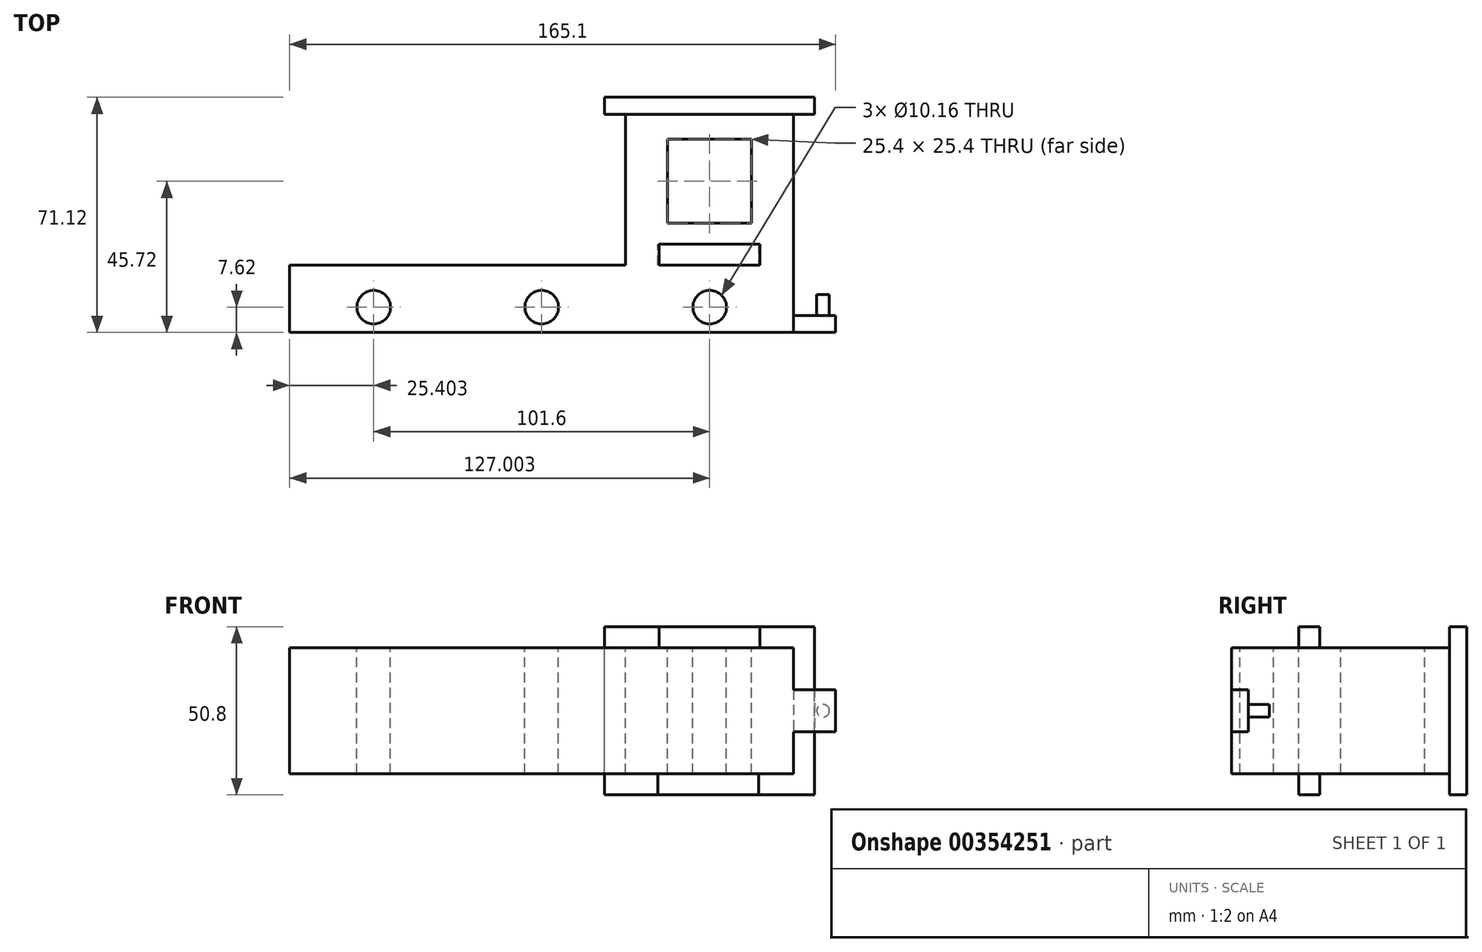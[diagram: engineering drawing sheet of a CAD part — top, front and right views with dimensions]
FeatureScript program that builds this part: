
annotation { "Feature Type Name" : "Feature", "Feature Type Description" : "" }
export const myFeature = defineFeature(function(context is Context, id is Id, definition is map)
    precondition{}
    {
        {
            var Q0;
            Q0=qCreatedBy(makeId("Front.planeOp"),FACE);
            var sketch = newSketch(context, id + "F0", { "sketchPlane" : qUnion([Q0])});
            skLineSegment(sketch, "E0.bottom", {"start": v(-68.46, 19.52) * mm, "end": v(83.94, 19.52) * mm});
            skLineSegment(sketch, "E0.top", {"start": v(-68.46, -18.58) * mm, "end": v(83.94, -18.58) * mm});
            skLineSegment(sketch, "E0.left", {"start": v(-68.46, 19.52) * mm, "end": v(-68.46, -18.58) * mm});
            skLineSegment(sketch, "E0.right", {"start": v(83.94, 19.52) * mm, "end": v(83.94, -18.58) * mm});
            skSolve(sketch);
        }
        {
            var Q0;
            Q0 = qSketchRegion(id + "F0", true);
            extrude(context, id + "F1", {"entities" : qUnion([Q0]), "depth" : 20.32 * mm});
        }
        {
            var Q0;
            Q0=makeQuery(id+"F1.opExtrude","CAP_FACE",FACE,{"disambiguationData":[OSD([sQuery(id+"F0.wireOp",EDGE,"E0.bottom"),sQuery(id+"F0.wireOp",EDGE,"E0.top"),sQuery(id+"F0.wireOp",EDGE,"E0.left"),sQuery(id+"F0.wireOp",EDGE,"E0.right")])],"isStart":true});
            var sketch = newSketch(context, id + "F2", { "sketchPlane" : qUnion([Q0])});
            skLineSegment(sketch, "E1", {"start": v(-33.14, -18.58) * mm, "end": v(-33.14, 19.52) * mm});
            skSolve(sketch);
        }
        {
            var Q0;
            {var subQ0=sQuery(id+"F2.wireOp",EDGE,"E1");Q0=makeQuery(id+"F2.imprint","IMPRINT",FACE,{"disambiguationData":[TD([[makeQuery(id+"F2.imprint","IMPRINT",EDGE,{"derivedFrom":subQ0}),1.0]])]});}
            extrude(context, id + "F3", {"entities" : qUnion([Q0]), "operationType" : NewBodyOperationType.ADD, "depth" : 50.8 * mm});
        }
        {
            var Q0;
            {var subQ0=sQuery(id+"F0.wireOp",EDGE,"E0.bottom");Q0=makeQuery(id+"F3.boolean.opBoolean","MERGE",FACE,{"derivedFrom":[makeQuery(id+"F1.opExtrude","SWEPT_FACE",FACE,{"disambiguationData":[OSD([subQ0])]}),makeQuery(id+"F3.opExtrude","SWEPT_FACE",FACE,{"disambiguationData":[OSD([subQ0])]})]});}
            var sketch = newSketch(context, id + "F4", { "sketchPlane" : qUnion([Q0])});
            skLineSegment(sketch, "E2.bottom", {"start": v(45.84, 38.1) * mm, "end": v(71.24, 38.1) * mm});
            skLineSegment(sketch, "E2.top", {"start": v(45.84, 12.7) * mm, "end": v(71.24, 12.7) * mm});
            skLineSegment(sketch, "E2.left", {"start": v(45.84, 38.1) * mm, "end": v(45.84, 12.7) * mm});
            skLineSegment(sketch, "E2.right", {"start": v(71.24, 38.1) * mm, "end": v(71.24, 12.7) * mm});
            skSolve(sketch);
        }
        {
            var Q0;
            Q0 = qSketchRegion(id + "F4", true);
            extrude(context, id + "F5", {"entities" : qUnion([Q0]), "operationType" : NewBodyOperationType.REMOVE, "endBound" : BoundingType.THROUGH_ALL, "oppositeDirection" : true, "depth" : 25.4 * mm});
        }
        {
            var Q0;
            {var subQ0=sQuery(id+"F0.wireOp",EDGE,"E0.bottom");Q0=makeQuery(id+"F3.boolean.opBoolean","MERGE",FACE,{"derivedFrom":[makeQuery(id+"F1.opExtrude","SWEPT_FACE",FACE,{"disambiguationData":[OSD([subQ0])]}),makeQuery(id+"F3.opExtrude","SWEPT_FACE",FACE,{"disambiguationData":[OSD([subQ0])]})]});}
            var sketch = newSketch(context, id + "F6", { "sketchPlane" : qUnion([Q0])});
            skLineSegment(sketch, "E3.top", {"start": v(43.3, 0) * mm, "end": v(73.78, 0) * mm});
            skLineSegment(sketch, "E4.MirrorCS", {"start": v(43.3, 6.35) * mm, "end": v(73.78, 6.35) * mm});
            skLineSegment(sketch, "E5.MirrorCS", {"start": v(43.3, 6.35) * mm, "end": v(43.3, 0) * mm});
            skLineSegment(sketch, "E6.MirrorCS", {"start": v(73.78, 6.35) * mm, "end": v(73.78, 0) * mm});
            skLineSegment(sketch, "E7", {"start": v(73.78, 0) * mm, "end": v(43.3, 0) * mm});
            skSolve(sketch);
        }
        {
            var Q0;
            Q0 = qSketchRegion(id + "F6", true);
            extrude(context, id + "F7", {"entities" : qUnion([Q0]), "operationType" : NewBodyOperationType.ADD, "depth" : 6.35 * mm});
        }
        {
            var Q0;
            {var subQ0=sQuery(id+"F0.wireOp",EDGE,"E0.top");Q0=makeQuery(id+"F3.boolean.opBoolean","MERGE",FACE,{"derivedFrom":[makeQuery(id+"F1.opExtrude","SWEPT_FACE",FACE,{"disambiguationData":[OSD([subQ0])]}),makeQuery(id+"F3.opExtrude","SWEPT_FACE",FACE,{"disambiguationData":[OSD([subQ0])]})]});}
            var sketch = newSketch(context, id + "F8", { "sketchPlane" : qUnion([Q0])});
            skLineSegment(sketch, "E8.MirrorCS", {"start": v(42.87, -6.35) * mm, "end": v(73.35, -6.35) * mm});
            skLineSegment(sketch, "E9.MirrorCS", {"start": v(42.87, 0) * mm, "end": v(42.87, -6.35) * mm});
            skLineSegment(sketch, "E10.MirrorCS", {"start": v(73.35, -6.35) * mm, "end": v(73.35, 0) * mm});
            skLineSegment(sketch, "E11", {"start": v(73.35, 0) * mm, "end": v(42.87, 0) * mm});
            skSolve(sketch);
        }
        {
            var Q0;
            Q0 = qSketchRegion(id + "F8", true);
            extrude(context, id + "F9", {"entities" : qUnion([Q0]), "operationType" : NewBodyOperationType.ADD, "depth" : 6.35 * mm});
        }
        {
            var Q0;
            {var subQ0=sQuery(id+"F0.wireOp",EDGE,"E0.right");Q0=makeQuery(id+"F3.boolean.opBoolean","MERGE",FACE,{"derivedFrom":[makeQuery(id+"F1.opExtrude","SWEPT_FACE",FACE,{"disambiguationData":[OSD([subQ0])]}),makeQuery(id+"F3.opExtrude","SWEPT_FACE",FACE,{"disambiguationData":[OSD([subQ0])]})]});}
            var sketch = newSketch(context, id + "F10", { "sketchPlane" : qUnion([Q0])});
            skLineSegment(sketch, "E12", {"start": v(45.65, -18.58) * mm, "end": v(45.65, 19.52) * mm});
            skSolve(sketch);
        }
        {
            var Q0;
            {var subQ0=sQuery(id+"F10.wireOp",EDGE,"E12");Q0=makeQuery(id+"F10.imprint","IMPRINT",FACE,{"disambiguationData":[TD([[makeQuery(id+"F10.imprint","IMPRINT",EDGE,{"derivedFrom":subQ0}),-1.0]])]});}
            extrude(context, id + "F11", {"entities" : qUnion([Q0]), "operationType" : NewBodyOperationType.ADD, "depth" : 6.35 * mm});
        }
        {
            var Q0;
            Q0=makeQuery(id+"F6.imprint","IMPRINT",FACE,{"disambiguationData":[TD([[makeQuery(id+"F6.imprint","IMPRINT",EDGE,{"derivedFrom":sQuery(id+"F6.wireOp",EDGE,"E4.MirrorCS")}),1.0]])]});
            var sketch = newSketch(context, id + "F12", { "sketchPlane" : qUnion([Q0])});
            skLineSegment(sketch, "E13", {"start": v(83.94, 45.65) * mm, "end": v(33.14, 45.65) * mm});
            skSolve(sketch);
        }
        {
            var Q0;
            {var subQ0=sQuery(id+"F12.wireOp",EDGE,"E13");Q0=makeQuery(id+"F12.imprint","IMPRINT",FACE,{"disambiguationData":[TD([[makeQuery(id+"F12.imprint","IMPRINT",EDGE,{"derivedFrom":subQ0}),-1.0]])]});}
            extrude(context, id + "F13", {"entities" : qUnion([Q0]), "operationType" : NewBodyOperationType.ADD, "depth" : 6.35 * mm});
        }
        {
            var Q0;
            Q0=makeQuery(id+"F13.opExtrude","SWEPT_FACE",FACE,{"disambiguationData":[OSD([sQuery(id+"F0.wireOp",EDGE,"E0.bottom"),sQuery(id+"F0.wireOp",EDGE,"E0.right")])]});
            extrude(context, id + "F14", {"entities" : qUnion([Q0]), "operationType" : NewBodyOperationType.ADD, "depth" : 6.35 * mm});
        }
        {
            var Q0;
            {var subQ0=sQuery(id+"F0.wireOp",EDGE,"E0.top");Q0=makeQuery(id+"F11.boolean.opBoolean","MERGE",FACE,{"derivedFrom":[makeQuery(id+"F3.boolean.opBoolean","MERGE",FACE,{"derivedFrom":[makeQuery(id+"F1.opExtrude","SWEPT_FACE",FACE,{"disambiguationData":[OSD([subQ0])]}),makeQuery(id+"F3.opExtrude","SWEPT_FACE",FACE,{"disambiguationData":[OSD([subQ0])]})]}),makeQuery(id+"F11.opExtrude","SWEPT_FACE",FACE,{"disambiguationData":[OSD([subQ0,sQuery(id+"F0.wireOp",EDGE,"E0.right")])]})]});}
            var sketch = newSketch(context, id + "F15", { "sketchPlane" : qUnion([Q0])});
            skLineSegment(sketch, "E14", {"start": v(83.94, -45.65) * mm, "end": v(33.14, -45.65) * mm});
            skSolve(sketch);
        }
        {
            var Q0;
            {var subQ3=sQuery(id+"F15.wireOp",EDGE,"E14");Q0=makeQuery(id+"F15.imprint","IMPRINT",FACE,{"disambiguationData":[TD([[makeQuery(id+"F15.imprint","IMPRINT",EDGE,{"derivedFrom":subQ3}),1.0]])]});}
            extrude(context, id + "F16", {"entities" : qUnion([Q0]), "operationType" : NewBodyOperationType.ADD, "depth" : 6.35 * mm});
        }
        {
            var Q0;
            {var subQ0=sQuery(id+"F2.wireOp",EDGE,"E1");Q0=makeQuery(id+"F16.boolean.opBoolean","MERGE",FACE,{"derivedFrom":[makeQuery(id+"F13.boolean.opBoolean","MERGE",FACE,{"derivedFrom":[makeQuery(id+"F3.opExtrude","SWEPT_FACE",FACE,{"disambiguationData":[OSD([subQ0])]}),makeQuery(id+"F13.opExtrude","SWEPT_FACE",FACE,{"disambiguationData":[OSD([sQuery(id+"F0.wireOp",EDGE,"E0.bottom"),subQ0])]})]}),makeQuery(id+"F16.opExtrude","SWEPT_FACE",FACE,{"disambiguationData":[OSD([sQuery(id+"F0.wireOp",EDGE,"E0.top"),subQ0])]})]});}
            var sketch = newSketch(context, id + "F17", { "sketchPlane" : qUnion([Q0])});
            skLineSegment(sketch, "E15", {"start": v(-45.65, -18.58) * mm, "end": v(-45.65, 19.52) * mm});
            skSolve(sketch);
        }
        {
            var Q0;
            Q0=makeQuery(id+"F17.imprint","IMPRINT",FACE,{"disambiguationData":[TD([[makeQuery(id+"F17.imprint","IMPRINT",EDGE,{"derivedFrom":sQuery(id+"F17.wireOp",EDGE,"E15")}),1.0]])]});
            extrude(context, id + "F18", {"entities" : qUnion([Q0]), "operationType" : NewBodyOperationType.ADD, "depth" : 6.35 * mm});
        }
        {
            var Q0;
            Q0=makeQuery(id+"F6.imprint","IMPRINT",FACE,{"disambiguationData":[TD([[makeQuery(id+"F6.imprint","IMPRINT",EDGE,{"derivedFrom":sQuery(id+"F6.wireOp",EDGE,"E4.MirrorCS")}),1.0]])]});
            var sketch = newSketch(context, id + "F19", { "sketchPlane" : qUnion([Q0])});
            skCircle(sketch, "E16", {"center": v(-43.06, -12.7) * mm, "radius": 5.08 * mm});
            skCircle(sketch, "E17", {"center": v(7.74, -12.7) * mm, "radius": 5.08 * mm});
            skCircle(sketch, "E18", {"center": v(58.54, -12.7) * mm, "radius": 5.08 * mm});
            skSolve(sketch);
        }
        {
            var Q0;
            Q0 = qSketchRegion(id + "F19", true);
            extrude(context, id + "F20", {"entities" : qUnion([Q0]), "operationType" : NewBodyOperationType.REMOVE, "endBound" : BoundingType.THROUGH_ALL, "oppositeDirection" : true, "depth" : 25.4 * mm});
        }
        {
            var Q0;
            {var subQ0=sQuery(id+"F0.wireOp",EDGE,"E0.right");Q0=makeQuery(id+"F3.boolean.opBoolean","MERGE",FACE,{"derivedFrom":[makeQuery(id+"F1.opExtrude","SWEPT_FACE",FACE,{"disambiguationData":[OSD([subQ0])]}),makeQuery(id+"F3.opExtrude","SWEPT_FACE",FACE,{"disambiguationData":[OSD([subQ0])]})]});}
            var sketch = newSketch(context, id + "F21", { "sketchPlane" : qUnion([Q0])});
            skLineSegment(sketch, "E19.bottom", {"start": v(-15.24, 6.82) * mm, "end": v(-20.32, 6.82) * mm});
            skLineSegment(sketch, "E19.top", {"start": v(-15.24, -5.88) * mm, "end": v(-20.32, -5.88) * mm});
            skLineSegment(sketch, "E19.left", {"start": v(-15.24, 6.82) * mm, "end": v(-15.24, -5.88) * mm});
            skLineSegment(sketch, "E19.right", {"start": v(-20.32, 6.82) * mm, "end": v(-20.32, -5.88) * mm});
            skSolve(sketch);
        }
        {
            var Q0;
            Q0=makeQuery(id+"F21.imprint","IMPRINT",FACE,{"disambiguationData":[TD([[makeQuery(id+"F21.imprint","IMPRINT",EDGE,{"derivedFrom":sQuery(id+"F21.wireOp",EDGE,"E19.bottom")}),1.0]])]});
            extrude(context, id + "F22", {"entities" : qUnion([Q0]), "operationType" : NewBodyOperationType.ADD, "depth" : 12.7 * mm});
        }
        {
            var Q0;
            Q0=makeQuery(id+"F22.opExtrude","SWEPT_FACE",FACE,{"disambiguationData":[OSD([sQuery(id+"F21.wireOp",EDGE,"E19.left")])]});
            var sketch = newSketch(context, id + "F23", { "sketchPlane" : qUnion([Q0])});
            skCircle(sketch, "E20", {"center": v(-92.83, 0.47) * mm, "radius": 1.9 * mm});
            skSolve(sketch);
        }
        {
            var Q0;
            Q0 = qSketchRegion(id + "F23", true);
            extrude(context, id + "F24", {"entities" : qUnion([Q0]), "operationType" : NewBodyOperationType.ADD, "depth" : 6.35 * mm});
        }
    });
